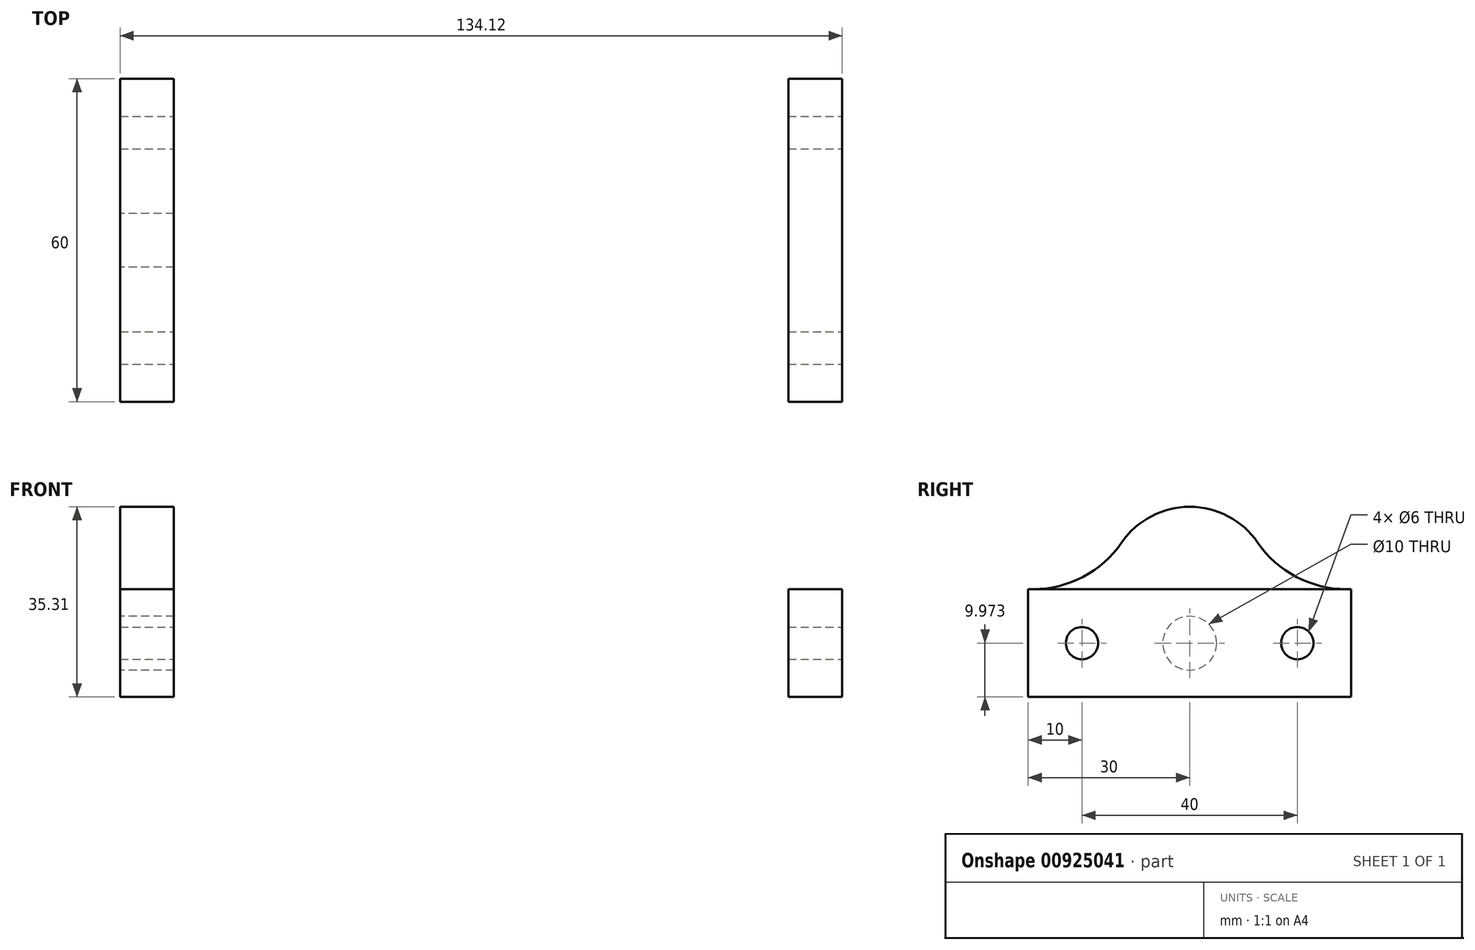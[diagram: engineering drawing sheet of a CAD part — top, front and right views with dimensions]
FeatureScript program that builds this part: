
annotation { "Feature Type Name" : "Feature", "Feature Type Description" : "" }
export const myFeature = defineFeature(function(context is Context, id is Id, definition is map)
    precondition{}
    {
        {
            var Q0;
            Q0=qCreatedBy(makeId("Top.planeOp"),FACE);
            var sketch = newSketch(context, id + "F0", { "sketchPlane" : qUnion([Q0])});
            skLineSegment(sketch, "E0", {"start": v(0, 0) * mm, "end": v(-67.06, 0) * mm});
            skLineSegment(sketch, "E1", {"start": v(-67.06, 0) * mm, "end": v(0, 0) * mm, "construction": true});
            skLineSegment(sketch, "E2.bottom", {"start": v(-67.06, 0) * mm, "end": v(-57.06, 0) * mm});
            skLineSegment(sketch, "E2.top", {"start": v(-67.06, 30) * mm, "end": v(-57.06, 30) * mm});
            skLineSegment(sketch, "E2.left", {"start": v(-67.06, 0) * mm, "end": v(-67.06, 30) * mm});
            skLineSegment(sketch, "E2.right", {"start": v(-57.06, 0) * mm, "end": v(-57.06, 30) * mm});
            skLineSegment(sketch, "E3.MirrorCS", {"start": v(-57.06, 0) * mm, "end": v(-57.06, -30) * mm});
            skLineSegment(sketch, "E4.MirrorCS", {"start": v(-67.06, -30) * mm, "end": v(-57.06, -30) * mm});
            skLineSegment(sketch, "E5.MirrorCS", {"start": v(-67.06, 0) * mm, "end": v(-67.06, -30) * mm});
            skLineSegment(sketch, "E6", {"start": v(0, 0) * mm, "end": v(0, 38.76) * mm, "construction": true});
            skLineSegment(sketch, "E7.MirrorCS", {"start": v(67.06, 30) * mm, "end": v(57.06, 30) * mm});
            skLineSegment(sketch, "E8.MirrorCS", {"start": v(57.06, 0) * mm, "end": v(57.06, 30) * mm});
            skLineSegment(sketch, "E9.MirrorCS", {"start": v(67.06, 0) * mm, "end": v(67.06, 30) * mm});
            skLineSegment(sketch, "E10.MirrorCS", {"start": v(67.06, 0) * mm, "end": v(67.06, -30) * mm});
            skLineSegment(sketch, "E11.MirrorCS", {"start": v(57.06, 0) * mm, "end": v(57.06, -30) * mm});
            skLineSegment(sketch, "E12.MirrorCS", {"start": v(67.06, -30) * mm, "end": v(57.06, -30) * mm});
            skSolve(sketch);
        }
        {
            var Q0;
            Q0=makeQuery(id+"F0.imprint","IMPRINT",FACE,{"disambiguationData":[TD([[makeQuery(id+"F0.imprint","IMPRINT",EDGE,{"derivedFrom":sQuery(id+"F0.wireOp",EDGE,"E2.top")}),-1.0]])]});
            var Q1;
            {var subQ2=sQuery(id+"F0.wireOp",EDGE,"E3.MirrorCS");Q1=makeQuery(id+"F0.imprint","IMPRINT",FACE,{"disambiguationData":[TD([[makeQuery(id+"F0.imprint","IMPRINT",EDGE,{"derivedFrom":subQ2}),-1.0]])]});}
            var Q2;
            Q2=makeQuery(id+"F0.imprint","IMPRINT",FACE,{"disambiguationData":[TD([[makeQuery(id+"F0.imprint","IMPRINT",EDGE,{"derivedFrom":sQuery(id+"F0.wireOp",EDGE,"E7.MirrorCS")}),1.0]])]});
            extrude(context, id + "F1", {"entities" : qUnion([Q0, Q1, Q2]), "depth" : 20 * mm, "offsetDistance" : 25 * mm});
        }
        {
            var Q0;
            Q0=makeQuery(id+"F1.opExtrude","SWEPT_FACE",FACE,{"disambiguationData":[OSD([sQuery(id+"F0.wireOp",EDGE,"E9.MirrorCS"),sQuery(id+"F0.wireOp",EDGE,"E10.MirrorCS")])]});
            var sketch = newSketch(context, id + "F2", { "sketchPlane" : qUnion([Q0])});
            skLineSegment(sketch, "E13", {"start": v(0, 7.97) * mm, "end": v(0, 34.97) * mm, "construction": true});
            skLineSegment(sketch, "E14", {"start": v(-23, 9.97) * mm, "end": v(-41.24, 9.97) * mm, "construction": true});
            skCircle(sketch, "E15", {"center": v(20, 9.97) * mm, "radius": 3 * mm});
            skCircle(sketch, "E16.MirrorC", {"center": v(-20, 9.97) * mm, "radius": 3 * mm});
            skSolve(sketch);
        }
        {
            var Q0;
            Q0 = qSketchRegion(id + "F2", true);
            extrude(context, id + "F3", {"entities" : qUnion([Q0]), "operationType" : NewBodyOperationType.REMOVE, "oppositeDirection" : true, "depth" : 175 * mm, "offsetDistance" : 25 * mm});
        }
        {
            var Q0;
            Q0=makeQuery(id+"F1.opExtrude","SWEPT_FACE",FACE,{"disambiguationData":[OSD([sQuery(id+"F0.wireOp",EDGE,"E2.left"),sQuery(id+"F0.wireOp",EDGE,"E5.MirrorCS")])]});
            var sketch = newSketch(context, id + "F4", { "sketchPlane" : qUnion([Q0])});
            skLineSegment(sketch, "E17", {"start": v(0, 20) * mm, "end": v(0, 0) * mm, "construction": true});
            skCircle(sketch, "E18", {"center": v(0, 10) * mm, "radius": 5 * mm});
            skArc(sketch, "E19", {"start": v(12.62, 28.67) * mm, "mid": v(0, 35.3) * mm, "end": v(-12.62, 28.67) * mm});
            skLineSegment(sketch, "E20", {"start": v(-30, 20) * mm, "end": v(-29.1, 20) * mm});
            skLineSegment(sketch, "E21.trimOffspring", {"start": v(29.1, 20) * mm, "end": v(30, 20) * mm});
            skPoint(sketch, "E22.visualSharp", {"position": v(-15.3, 20) * mm});
            skArc(sketch, "E22.filletArc", {"start": v(-29.1, 20) * mm, "mid": v(-19.79, 22.3) * mm, "end": v(-12.62, 28.67) * mm});
            skPoint(sketch, "E23.visualSharp", {"position": v(15.3, 20) * mm});
            skArc(sketch, "E23.filletArc", {"start": v(12.62, 28.67) * mm, "mid": v(19.79, 22.3) * mm, "end": v(29.1, 20) * mm});
            skSolve(sketch);
        }
        {
            var Q0;
            Q0=makeQuery(id+"F4.imprint","IMPRINT",FACE,{"disambiguationData":[TD([[makeQuery(id+"F4.imprint","IMPRINT",EDGE,{"derivedFrom":sQuery(id+"F4.wireOp",EDGE,"E19")}),1.0]])]});
            var Q1;
            Q1=makeQuery(id+"F1.opExtrude","SWEPT_FACE",FACE,{"disambiguationData":[OSD([sQuery(id+"F0.wireOp",EDGE,"E2.right"),sQuery(id+"F0.wireOp",EDGE,"E3.MirrorCS")])]});
            var Q2;
            Q2=makeQuery(id+"F1.opExtrude","SWEPT_FACE",FACE,{"disambiguationData":[OSD([sQuery(id+"F0.wireOp",EDGE,"E2.right"),sQuery(id+"F0.wireOp",EDGE,"E3.MirrorCS")])]});
            extrude(context, id + "F5", {"entities" : qUnion([Q0]), "operationType" : NewBodyOperationType.ADD, "endBound" : BoundingType.UP_TO_SURFACE, "oppositeDirection" : true, "depth" : 25 * mm, "endBoundEntityFace" : qUnion([Q1]), "offsetDistance" : 25 * mm});
        }
        {
            var Q0;
            {var subQ0=sQuery(id+"F0.wireOp",EDGE,"E5.MirrorCS");var subQ1=sQuery(id+"F0.wireOp",EDGE,"E2.left");Q0=makeQuery(id+"F5.boolean.opBoolean","MERGE",FACE,{"derivedFrom":[makeQuery(id+"F1.opExtrude","SWEPT_FACE",FACE,{"disambiguationData":[OSD([subQ1,subQ0])]}),makeQuery(id+"F5.opExtrude","CAP_FACE",FACE,{"disambiguationData":[OSD([subQ1,subQ0,sQuery(id+"F4.wireOp",EDGE,"E19"),sQuery(id+"F4.wireOp",EDGE,"E22.filletArc"),sQuery(id+"F4.wireOp",EDGE,"E23.filletArc")])],"isStart":true})]});}
            var sketch = newSketch(context, id + "F6", { "sketchPlane" : qUnion([Q0])});
            skLineSegment(sketch, "E24", {"start": v(-20, 9.97) * mm, "end": v(-20, 9.97) * mm});
            skCircle(sketch, "E25", {"center": v(0, 9.97) * mm, "radius": 5 * mm});
            skSolve(sketch);
        }
        {
            var Q0;
            Q0=makeQuery(id+"F6.imprint","IMPRINT",FACE,{"disambiguationData":[TD([[makeQuery(id+"F6.imprint","IMPRINT",EDGE,{"derivedFrom":sQuery(id+"F6.wireOp",EDGE,"E25")}),1.0]])]});
            extrude(context, id + "F7", {"entities" : qUnion([Q0]), "operationType" : NewBodyOperationType.REMOVE, "oppositeDirection" : true, "depth" : 31.6 * mm, "offsetDistance" : 25 * mm});
        }
    });
